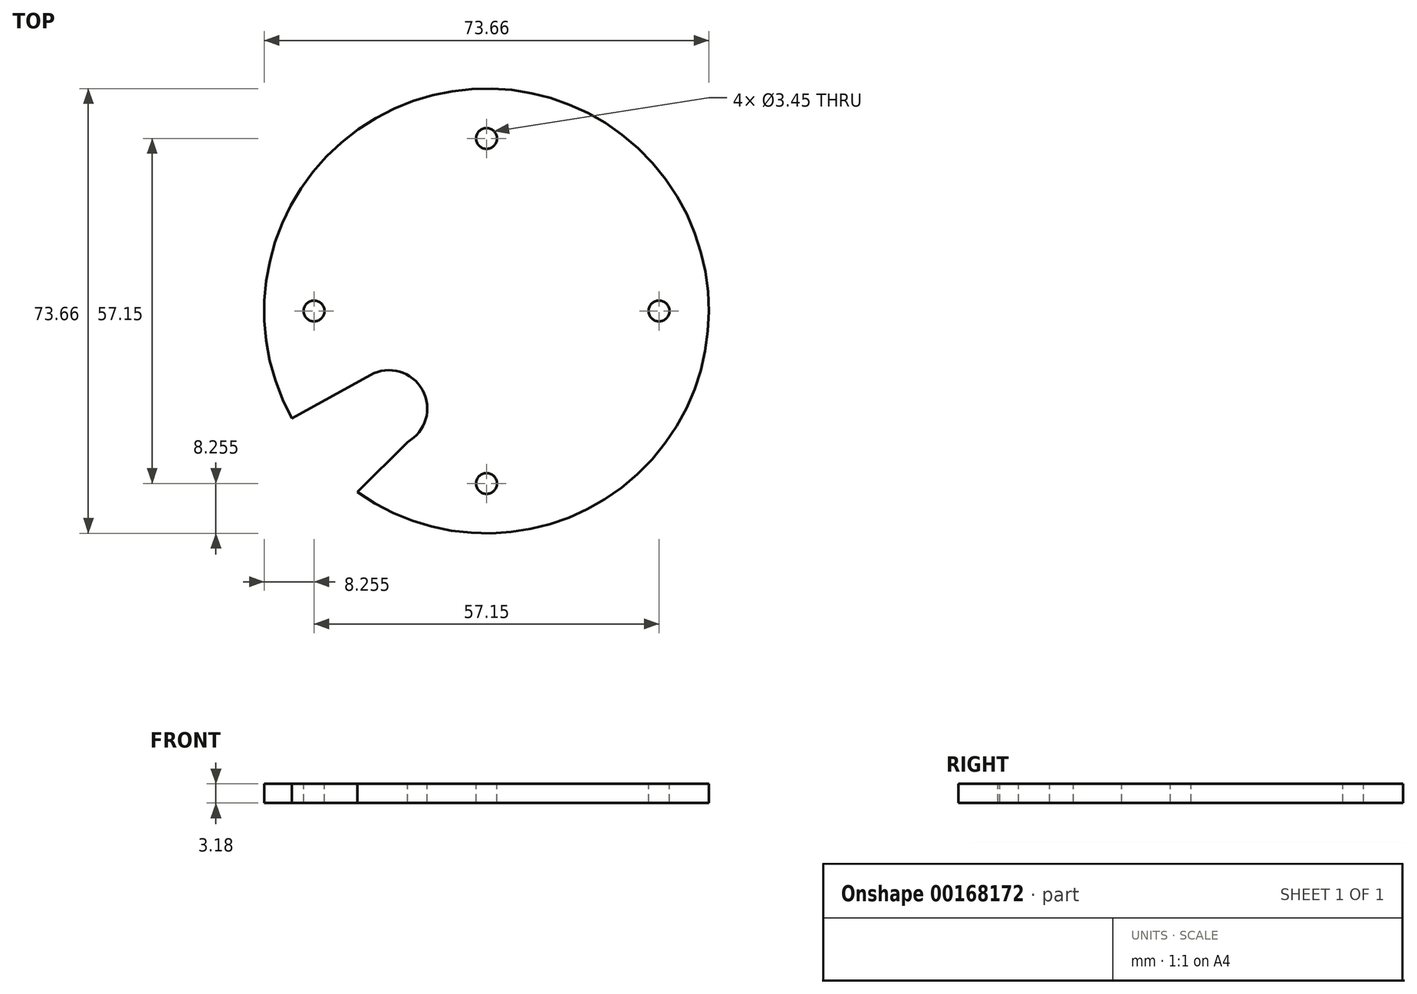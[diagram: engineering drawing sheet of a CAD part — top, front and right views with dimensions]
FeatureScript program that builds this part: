
annotation { "Feature Type Name" : "Feature", "Feature Type Description" : "" }
export const myFeature = defineFeature(function(context is Context, id is Id, definition is map)
    precondition{}
    {
        {
            var Q0;
            Q0=qCreatedBy(makeId("Top.planeOp"),FACE);
            var sketch = newSketch(context, id + "F0", { "sketchPlane" : qUnion([Q0])});
            skCircle(sketch, "E0", {"center": v(0, 0) * mm, "radius": 36.83 * mm});
            skSolve(sketch);
        }
        {
            var Q0;
            Q0=makeQuery(id+"F0.imprint","IMPRINT",FACE,{"disambiguationData":[TD([[makeQuery(id+"F0.imprint","IMPRINT",EDGE,{"derivedFrom":sQuery(id+"F0.wireOp",EDGE,"E0")}),1.0]])]});
            extrude(context, id + "F1", {"entities" : qUnion([Q0]), "depth" : 3.17 * mm});
        }
        {
            var Q0;
            {var subQ0=makeQuery(id+"FhJubWmbG7UBd7M_1.boolean.opBoolean","COPY",FACE,{"derivedFrom":makeQuery(id+"FhJubWmbG7UBd7M_1.opExtrude","SWEPT_FACE",FACE,{"disambiguationData":[OSD([sQuery(id+"FRuIeaWD6VeLny9_1.wireOp",EDGE,"idePJaX5-tPPE-BKw2-N1m4-zZUQrY6AHjir")])]})});Q0=makeQuery(id+"FOQC5dfjhO448EJ_1.boolean.opBoolean","SPLIT",FACE,{"disambiguationData":[TD([subQ0])],"derivedFrom":makeQuery(id+"FkcieFRIapZdHPD_1.boolean.opBoolean","SPLIT",FACE,{"disambiguationData":[TD([subQ0])],"derivedFrom":makeQuery(id+"F1.opExtrude","CAP_FACE",FACE,{"disambiguationData":[OSD([sQuery(id+"F0.wireOp",EDGE,"E0")])],"isStart":false})})});}
            var sketch = newSketch(context, id + "F2", { "sketchPlane" : qUnion([Q0])});
            skCircle(sketch, "E1", {"center": v(0, 0) * mm, "radius": 28.58 * mm, "construction": true});
            skLineSegment(sketch, "E2", {"start": v(0, 0) * mm, "end": v(28.58, 0) * mm, "construction": true});
            skPoint(sketch, "E3", {"position": v(28.58, 0) * mm});
            skLineSegment(sketch, "E4", {"start": v(0, 0) * mm, "end": v(-28.58, 0) * mm, "construction": true});
            skPoint(sketch, "E5", {"position": v(-28.58, 0) * mm});
            skPoint(sketch, "E6.1.0", {"position": v(0, -28.58) * mm});
            skPoint(sketch, "E6.3.0", {"position": v(0, 28.58) * mm});
            skSolve(sketch);
        }
        {
            var Q0;
            Q0=sQuery(id+"F2.wireOp",VERTEX,"E5");
            var Q1;
            Q1=sQuery(id+"F2.wireOp",VERTEX,"E6.3.0");
            var Q2;
            Q2=sQuery(id+"F2.wireOp",VERTEX,"E3");
            var Q3;
            Q3=sQuery(id+"F2.wireOp",VERTEX,"E6.1.0");
            var Q4;
            Q4=makeQuery(id+"F1.opExtrude","SWEPT_BODY",BODY,{"disambiguationData":[OSD([sQuery(id+"F0.wireOp",EDGE,"E0")])]});
            hole(context, id + "F3", {"style" : HoleStyle.SIMPLE, "endStyle" : HoleEndStyle.BLIND, "standardTappedOrClearance" : lookupTablePath({ "standard" : "ANSI", "engagement" : "75%", "pitch" : "32 tpi", "size" : "#8", "type" : "Tapped" }), "standardBlindInLast" : lookupTablePath({ "standard" : "ANSI", "engagement" : "75%", "pitch" : "32 tpi", "size" : "#8", "type" : "Tapped" }), "holeDiameter" : 3.45 * mm, "holeDepth" : 11.43 * mm, "locations" : qUnion([Q0, Q1, Q2, Q3]), "scope" : qUnion([Q4]), "majorDiameter" : 4.17 * mm});
        }
        {
            var Q0;
            Q0=makeQuery(id+"F1.opExtrude","CAP_FACE",FACE,{"disambiguationData":[OSD([sQuery(id+"F0.wireOp",EDGE,"E0")])],"isStart":false});
            var sketch = newSketch(context, id + "F4", { "sketchPlane" : qUnion([Q0])});
            skCircle(sketch, "E7", {"center": v(-16.16, -16.16) * mm, "radius": 6.35 * mm});
            skLineSegment(sketch, "E8", {"start": v(-16.16, -16.16) * mm, "end": v(0, 0) * mm, "construction": true});
            skSolve(sketch);
        }
        {
            var Q0;
            Q0=qSketchRegion(id+"F4",true);
            extrude(context, id + "F5", {"entities" : qUnion([Q0]), "operationType" : NewBodyOperationType.REMOVE, "endBound" : BoundingType.THROUGH_ALL, "oppositeDirection" : true, "depth" : 25.4 * mm});
        }
        {
            var Q0;
            Q0=makeQuery(id+"F1.opExtrude","CAP_FACE",FACE,{"disambiguationData":[OSD([sQuery(id+"F0.wireOp",EDGE,"E0")])],"isStart":false});
            var sketch = newSketch(context, id + "F6", { "sketchPlane" : qUnion([Q0])});
            skLineSegment(sketch, "E9", {"start": v(-19.23, -10.6) * mm, "end": v(0, 0) * mm, "construction": true});
            skLineSegment(sketch, "E10", {"start": v(-10.6, -19.23) * mm, "end": v(0, 0) * mm, "construction": true});
            skLineSegment(sketch, "E11", {"start": v(-19.23, -10.6) * mm, "end": v(-10.6, -19.23) * mm});
            skLineSegment(sketch, "E12", {"start": v(-10.6, -19.23) * mm, "end": v(-21.37, -30) * mm});
            skLineSegment(sketch, "E13", {"start": v(-19.23, -10.6) * mm, "end": v(-32.25, -17.78) * mm});
            skLineSegment(sketch, "E14", {"start": v(-32.25, -17.78) * mm, "end": v(-39.34, -25.8) * mm});
            skLineSegment(sketch, "E15", {"start": v(-39.34, -25.8) * mm, "end": v(-21.37, -30) * mm});
            skSolve(sketch);
        }
        {
            var Q0;
            Q0=qSketchRegion(id+"F6",true);
            extrude(context, id + "F7", {"entities" : qUnion([Q0]), "operationType" : NewBodyOperationType.REMOVE, "endBound" : BoundingType.THROUGH_ALL, "oppositeDirection" : true, "depth" : 25.4 * mm});
        }
    });
